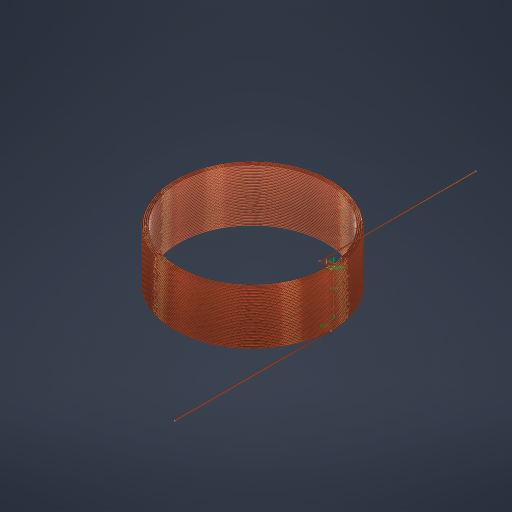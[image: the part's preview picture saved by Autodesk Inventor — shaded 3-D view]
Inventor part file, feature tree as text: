
AUTODESK INVENTOR PART (.ipt)
format: ipt  version: 2024.2 (Build 282272000, 272)  size: 3,403,264 bytes
history: native  units: mm
features: other x9, sketch x9, chamfer x8, sweep x4, extrude x1
ambient origin geometry x8: Origin, YZ Plane, XZ Plane, XY Plane, X Axis, Y Axis, Z Axis, Center Point
bodies: Volumenkörper1 (feature_tree), Volumenkörper2 (feature_tree), Volumenkörper3 (feature_tree), Volumenkörper4 (feature_tree), Volumenkörper5 (feature_tree), Volumenkörper6 (feature_tree), Volumenkörper7 (feature_tree), Volumenkörper8 (feature_tree), Volumenkörper9 (feature_tree)
feature tree (31):
  other  "Spirale1"
  other  "Spirale2"
  other  "Spirale3"
  other  "Spirale4"
  sweep  "Sweeping1"
  other  "3D-Skizze7"
  sketch  "Skizze15"  dims[d26=0.101mm d27=4.0mm d28=400.0mm d29=0.0mm d30=90.0deg d31=90.0deg d32=0.0mm d33=0.0mm]
  sweep  "Sweeping2"
  sweep  "Sweeping3"
  chamfer  "Fasen4"  Distance=0.7mm
  chamfer  "Fasen5"  [1 undecoded]
  chamfer  "Fasen6"  Distance=0.39mm
  chamfer  "Fasen7"  Distance=0.59mm
  chamfer  "Fasen8"  Distance=4.04mm
  chamfer  "Fasen9"  Distance=0.57mm
  extrude  "Extrusion1"  TaperAngle=0.0deg  [1 undecoded]
  chamfer  "Fasen10"  Distance=0.37mm
  sweep  "Sweeping4"
  chamfer  "Fasen11"  Distance=0.33mm
  other  "Kombinieren3"
  sketch  "Skizze1"  dims[d0=0.1mm d1=6.0mm]
  other  "3D-Skizze5"
  sketch  "Skizze14"  dims[d16=0.1mm d17=5.6995mm d18=0.101mm d19=4.0mm d20=400.0mm d21=0.0mm d22=90.0deg d23=90.0deg d24=0.0mm d25=0.0mm]
  sketch  "Skizze16"  dims[d34=0.101mm d35=4.0mm d36=400.0mm d37=0.0mm d38=90.0deg d39=90.0deg d40=0.0mm d41=0.0mm d45=0.5mm]
  other  "3D-Skizze8"
  sketch  "Skizze17"  dims[d46=0.8mm]
  sketch  "Skizze18"  dims[d47=4.04mm]
  other  "3D-Skizze9"
  sketch  "Skizze19"  dims[d48=0.8mm d49=0.7mm d50=0.0mm d51=0.0mm d57=0.39mm d58=0.59mm d59=4.04mm d60=0.57mm d61=0.0mm d62=0.0mm d65=0.37mm d66=4.04mm d67=0.33mm d68=0.27mm d69=0.0mm d70=0.0mm d71=0.08mm d72=0.08mm d73=0.08mm d83=0.01mm d84=2.0mm d85=45.0deg d86=0.01mm d87=2.0mm d88=45.0deg d89=0.01mm d90=2.0mm d91=45.0deg d92=0.01mm d93=2.0mm d94=45.0deg d95=0.01mm d96=2.0mm d97=45.0deg d98=0.01mm d99=2.0mm d100=45.0deg d101=0.08mm d102=12.0mm d103=0.0mm d104=0.01mm d105=2.0mm d106=45.0deg d107=0.17mm d108=0.7mm d109=12.0mm d110=0.08mm d111=0.0mm d112=0.0mm d113=0.01mm d114=2.0mm d115=45.0deg]
  sketch  "Skizze3"  dims[d2=0.101mm d3=4.0mm d4=400.0mm d5=0.0mm d6=0.0mm d7=90.0deg d8=0.0mm d9=0.0mm d12=0.1mm d13=5.8995mm]
  sketch  "Skizze4"  dims[d14=0.1mm d15=5.7995mm]
note: 2 required parameter values undecoded (feature->parameter linkage not recoverable at this tier; creation-order binding heuristic only, values carry confidence <= 0.55)
